# Revit family: 2069354 Sylvania Lighting Fixture PIXER RECESSED 600X600 HE 4P 4000K DALI CB EM
name_source: partatom
category: Lighting Fixtures
revit_build: Autodesk Revit 2016 (Build: 20150220_1215(x64)
units: mm (PartAtom-declared; Revit-internal decimal feet)

## family parameters
Cut with Voids When Loaded = No
Host = Face
Light Source = No
OmniClass Number = 23.80.70.00
OmniClass Title = Lighting
Part Type = Normal
Room Calculation Point = No
Round Connector Dimension = Use Diameter
Shared = No

## types (2) — shared parameters
Assembly Code = D5020200
AssetType = Fixed
ClassificationName = Uniclass2015
ClassificationValue = EF_70_80
Default Elevation = 1219 mm
Description = PIXER RECESSED 600X600 HE 4P 4000K DALI CB EM is a high performance low glare office luminaire with individually adjustable light pods to enhance arhitectural design. Diffuser is made of optical grade polycarbonate with an optical film for high efficacy and excellent glare control. Suitable for offices where aesthetics is important. Ceiling recessed 600x600mm, White colour - RAL9010. DALI dimmable, 4000K Neutral White LED, CRI>80, chromaticity tolerance of 3-step MacAdam ellipse. Lumen package of 3750 lm, total power consumtion 25W, efficacy 150lm/W. Lumen maintenance of L90B10 at 61,000 hours. UGR<19. IK02, IP20. Electrical protection: Class II. Central Battery emergency version. Glow wire test 650°C.
DimmingControlOptions = Non dimmable
DocumentationLiterature = http://www.sylvania-lighting.com
ElectricShockClassification = Class II
IfcExportAs = IfcLightFixtureType
IfcExportType = IfcLightFixtureType
ImpactProtectionIndex = IK02
IngressProtection = IP20
InputNominalFrequency = 50/60 Hz
InputVoltage = 220-240V~
Keynote = 16500
Lamp = LED
LampColourRenderingIndex = 80
LampColourTemperature = 4000 K
LampMacAdamStep = 3
LampsType = LED
Length_SYL = 595 mm  [stored 1.9521 ft]
LightOutputRatio = 100
Manufacturer = Feilo Sylvania
ManufacturerName = Feilo Sylvania
Material = powder coated steel housing, polycarbonate diffuser
Material_1_SYL = PC/ABS Plastic
Model = PIXER RECESSED 600X600 HE 4P 4000K DALI CB EM
ModelNumber = 2069354
ModelReference = PIXER RECESSED 600X600 HE 4P 4000K DALI CB EM
Name = PIXER RECESSED 600X600 HE 4P 4000K DALI CB EM
NominalDepth = 595 mm  [stored 1.9521 ft]
NominalHeight = 75 mm
NominalLength = 595 mm  [stored 1.9521 ft]
PodXInstance_SYL = 2
PowerConsumption = 25 W
RadiusBody_SYL = 5 mm  [stored 0.0164042 ft]
Type Image = <None>
TypeName = PIXER RECESSED 600X600 HE 4P 4000K DALI CB EM
URL = http://www.sylvania-lighting.com
Voltage = 230 V
Weight = 6.0 kg
Width_SYL = 595 mm  [stored 1.9521 ft]
Xdistance_SYL = 149 mm
Xinstance_SYL = 4
Ydistance_SYL = 149 mm
Yinstance_SYL = 4
zero-valued in all types: Cost, PowerFactor

## per-type parameters (varying)
| type | Apparent Load | LampNominalLuminous | LuminousEfficacy | TypePod_SYL |
| 2069354 PIXER R 600 HE 4P 4K DALI CB EM | 25 VA | 3750 lm | 150 lm/W | Pixer Pod Square : 2069354 PIXER R 600 HE 4P 4K DALI CB EM |
| 2069354 PIXER R 600 HE 4P 4K DALI CB EM Emergency mode | 6 VA | 549.3 lm | 85.43 lm/W | Pixer Pod Square : 2069354 PIXER R 600 HE 4P 4K DALI CB EM Emergency mode |

note: [stored X ft] marks values corroborated as IEEE doubles in the binary element streams (Revit-internal decimal feet)

## geometry (parser evidence)
native form markers: Sweep x1
no freeform markers — native parametric forms only
